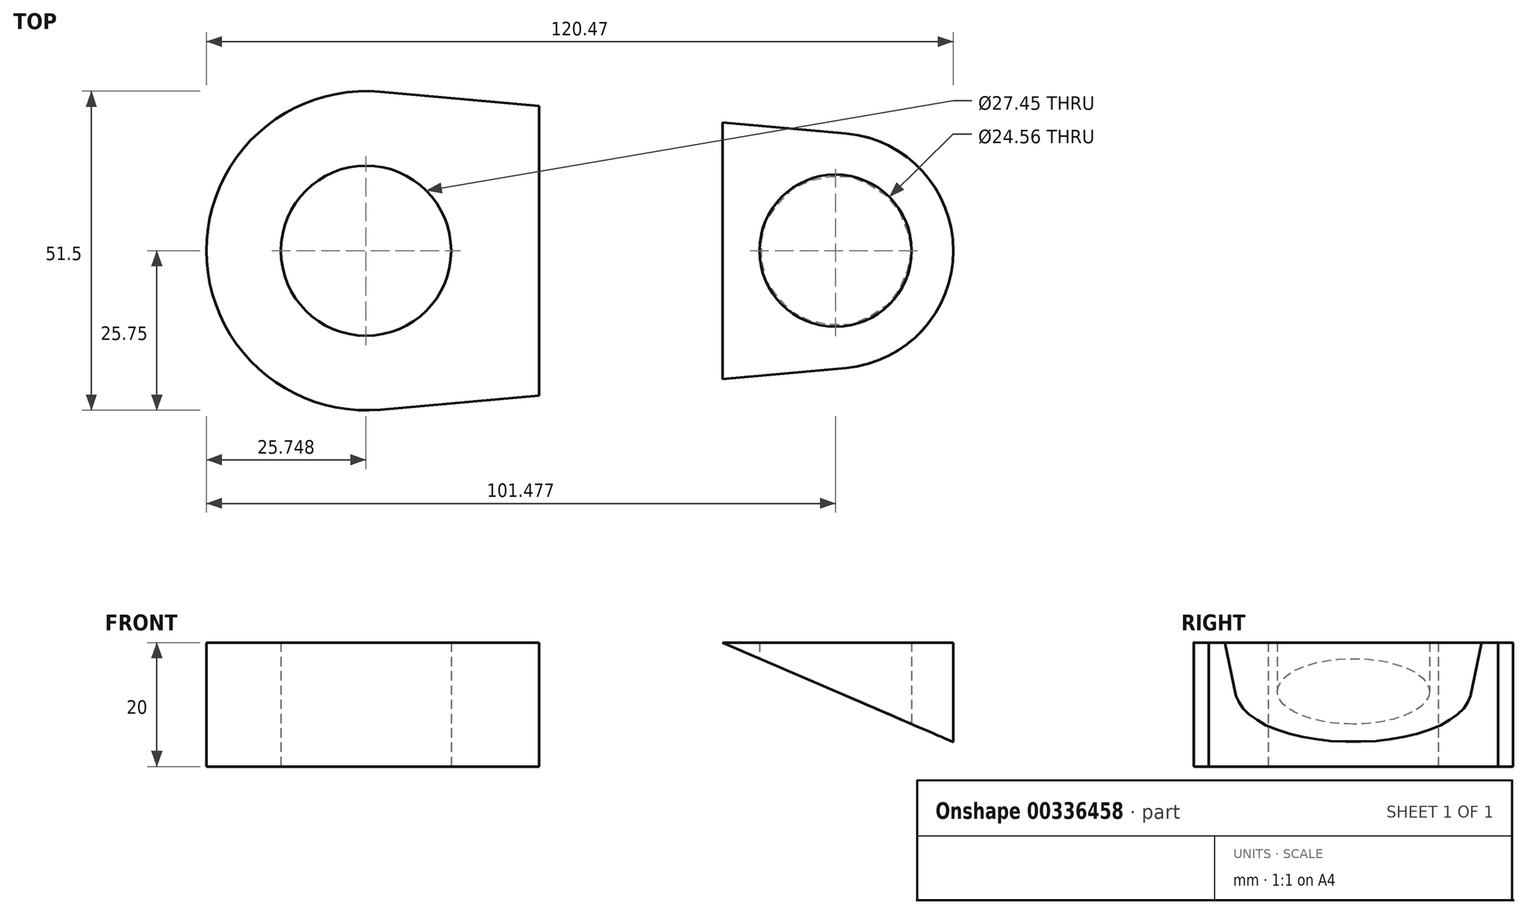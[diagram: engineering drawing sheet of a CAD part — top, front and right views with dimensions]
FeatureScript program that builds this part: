
annotation { "Feature Type Name" : "Feature", "Feature Type Description" : "" }
export const myFeature = defineFeature(function(context is Context, id is Id, definition is map)
    precondition{}
    {
        {
            var Q0;
            Q0=qCreatedBy(makeId("Top.planeOp"),FACE);
            var sketch = newSketch(context, id + "F0", { "sketchPlane" : qUnion([Q0])});
            skArc(sketch, "E0", {"start": v(28.56, -18.92) * mm, "mid": v(45.86, 0) * mm, "end": v(28.56, 18.92) * mm});
            skArc(sketch, "E1", {"start": v(-46.57, 25.64) * mm, "mid": v(-74.6, 0) * mm, "end": v(-46.57, -25.64) * mm});
            skLineSegment(sketch, "E2", {"start": v(28.56, -18.92) * mm, "end": v(-46.57, -25.64) * mm});
            skLineSegment(sketch, "E3", {"start": v(-46.57, 25.64) * mm, "end": v(28.56, 18.92) * mm});
            skCircle(sketch, "E4", {"center": v(-48.86, 0) * mm, "radius": 13.72 * mm});
            skCircle(sketch, "E5", {"center": v(26.87, 0) * mm, "radius": 12.28 * mm});
            skSolve(sketch);
        }
        {
            var Q0;
            Q0=makeQuery(id+"F0.imprint","IMPRINT",FACE,{"disambiguationData":[TD([[makeQuery(id+"F0.imprint","IMPRINT",EDGE,{"derivedFrom":sQuery(id+"F0.wireOp",EDGE,"E0")}),1.0]])]});
            extrude(context, id + "F1", {"entities" : qUnion([Q0]), "depth" : 20 * mm});
        }
        {
            var Q0;
            Q0=qCreatedBy(makeId("Front.planeOp"),FACE);
            var sketch = newSketch(context, id + "F2", { "sketchPlane" : qUnion([Q0])});
            skLineSegment(sketch, "E6", {"start": v(-20.96, 0) * mm, "end": v(-20.96, 32.77) * mm});
            skLineSegment(sketch, "E7", {"start": v(-20.96, 32.77) * mm, "end": v(55.06, 0) * mm});
            skLineSegment(sketch, "E8", {"start": v(55.06, 0) * mm, "end": v(-20.96, 0) * mm});
            skSolve(sketch);
        }
        {
            var Q0;
            Q0=makeQuery(id+"F2.imprint","IMPRINT",FACE,{"disambiguationData":[TD([[makeQuery(id+"F2.imprint","IMPRINT",EDGE,{"derivedFrom":sQuery(id+"F2.wireOp",EDGE,"E6")}),-1.0]])]});
            extrude(context, id + "F3", {"entities" : qUnion([Q0]), "operationType" : NewBodyOperationType.REMOVE, "endBound" : BoundingType.SYMMETRIC, "oppositeDirection" : true, "depth" : 50.42 * mm});
        }
    });
